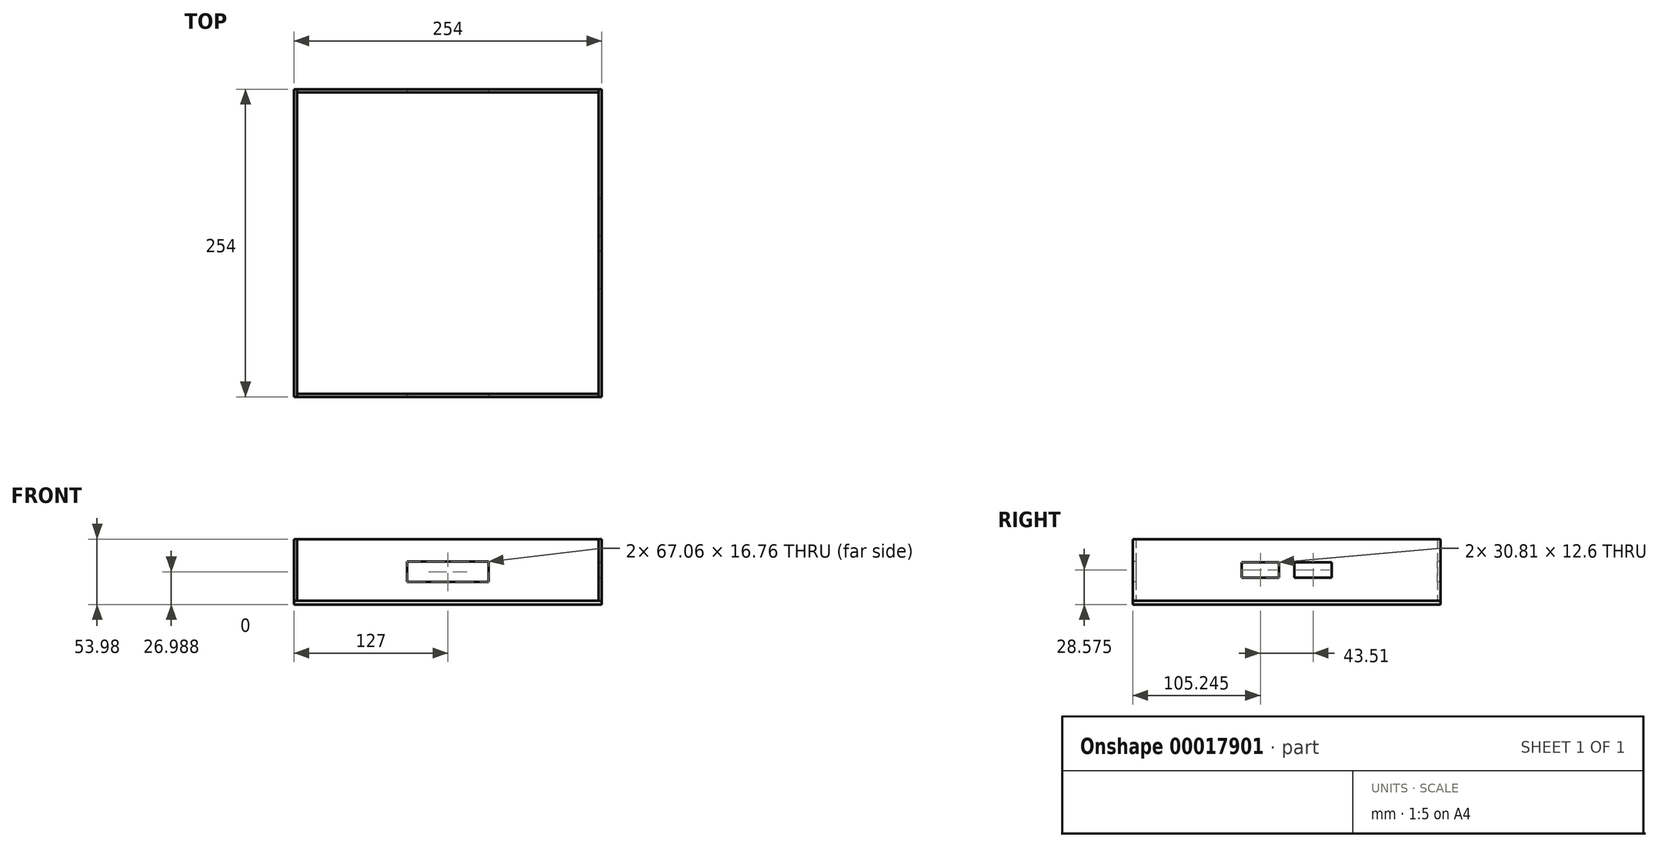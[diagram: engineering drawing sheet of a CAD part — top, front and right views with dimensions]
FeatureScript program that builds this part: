
annotation { "Feature Type Name" : "Feature", "Feature Type Description" : "" }
export const myFeature = defineFeature(function(context is Context, id is Id, definition is map)
    precondition{}
    {
        {
            var Q0;
            Q0=qCreatedBy(makeId("Top.planeOp"),FACE);
            var sketch = newSketch(context, id + "F0", { "sketchPlane" : qUnion([Q0])});
            skLineSegment(sketch, "E0.rect.bottom", {"start": v(-127, 127) * mm, "end": v(127, 127) * mm});
            skLineSegment(sketch, "E0.rect.top", {"start": v(-127, -127) * mm, "end": v(127, -127) * mm});
            skLineSegment(sketch, "E0.rect.left", {"start": v(-127, 127) * mm, "end": v(-127, -127) * mm});
            skLineSegment(sketch, "E0.rect.right", {"start": v(127, 127) * mm, "end": v(127, -127) * mm});
            skPoint(sketch, "E0.rect.middle", {"position": v(0, 0) * mm});
            skSolve(sketch);
        }
        {
            var Q0;
            Q0 = qSketchRegion(id + "F0", true);
            extrude(context, id + "F1", {"entities" : qUnion([Q0]), "depth" : 3.17 * mm});
        }
        {
            var Q0;
            Q0=makeQuery(id+"F1.opExtrude","CAP_FACE",FACE,{"disambiguationData":[OSD([sQuery(id+"F0.wireOp",EDGE,"E0.rect.bottom"),sQuery(id+"F0.wireOp",EDGE,"E0.rect.top"),sQuery(id+"F0.wireOp",EDGE,"E0.rect.left"),sQuery(id+"F0.wireOp",EDGE,"E0.rect.right")])],"isStart":false});
            var sketch = newSketch(context, id + "F2", { "sketchPlane" : qUnion([Q0])});
            skLineSegment(sketch, "E1.bottom", {"start": v(127, 127) * mm, "end": v(124.46, 127) * mm});
            skLineSegment(sketch, "E1.top", {"start": v(127, -127) * mm, "end": v(124.46, -127) * mm});
            skLineSegment(sketch, "E1.left", {"start": v(127, 127) * mm, "end": v(127, -127) * mm});
            skLineSegment(sketch, "E1.right", {"start": v(124.46, 127) * mm, "end": v(124.46, -127) * mm});
            skLineSegment(sketch, "E2.bottom", {"start": v(124.46, -127) * mm, "end": v(-124.46, -127) * mm});
            skLineSegment(sketch, "E2.top", {"start": v(124.46, -124.46) * mm, "end": v(-124.46, -124.46) * mm});
            skLineSegment(sketch, "E2.left", {"start": v(124.46, -127) * mm, "end": v(124.46, -124.46) * mm});
            skLineSegment(sketch, "E2.right", {"start": v(-124.46, -127) * mm, "end": v(-124.46, -124.46) * mm});
            skLineSegment(sketch, "E3.bottom", {"start": v(-127, -127) * mm, "end": v(-124.46, -127) * mm});
            skLineSegment(sketch, "E3.top", {"start": v(-127, 127) * mm, "end": v(-124.46, 127) * mm});
            skLineSegment(sketch, "E3.left", {"start": v(-127, -127) * mm, "end": v(-127, 127) * mm});
            skLineSegment(sketch, "E3.right", {"start": v(-124.46, -127) * mm, "end": v(-124.46, 127) * mm});
            skLineSegment(sketch, "E4.bottom", {"start": v(-124.46, 127) * mm, "end": v(124.46, 127) * mm});
            skLineSegment(sketch, "E4.top", {"start": v(-124.46, 124.46) * mm, "end": v(124.46, 124.46) * mm});
            skLineSegment(sketch, "E4.left", {"start": v(-124.46, 127) * mm, "end": v(-124.46, 124.46) * mm});
            skLineSegment(sketch, "E4.right", {"start": v(124.46, 127) * mm, "end": v(124.46, 124.46) * mm});
            skSolve(sketch);
        }
        {
            var Q0;
            {var subQ2=sQuery(id+"F2.wireOp",EDGE,"E2.bottom");Q0=makeQuery(id+"F2.imprint","IMPRINT",FACE,{"disambiguationData":[TD([[makeQuery(id+"F2.imprint","IMPRINT",EDGE,{"derivedFrom":subQ2}),1.0]])]});}
            extrude(context, id + "F3", {"entities" : qUnion([Q0]), "depth" : 50.8 * mm});
        }
        {
            var Q0;
            {var subQ3=sQuery(id+"F2.wireOp",EDGE,"E3.bottom");Q0=makeQuery(id+"F2.imprint","IMPRINT",FACE,{"disambiguationData":[TD([[makeQuery(id+"F2.imprint","IMPRINT",EDGE,{"derivedFrom":subQ3}),1.0]])]});}
            extrude(context, id + "F4", {"entities" : qUnion([Q0]), "depth" : 50.8 * mm});
        }
        {
            var Q0;
            Q0=makeQuery(id+"F2.imprint","IMPRINT",FACE,{"disambiguationData":[TD([[makeQuery(id+"F2.imprint","IMPRINT",EDGE,{"derivedFrom":sQuery(id+"F2.wireOp",EDGE,"E1.bottom")}),-1.0]])]});
            extrude(context, id + "F5", {"entities" : qUnion([Q0]), "depth" : 50.8 * mm});
        }
        {
            var Q0;
            Q0=makeQuery(id+"F2.imprint","IMPRINT",FACE,{"disambiguationData":[TD([[makeQuery(id+"F2.imprint","IMPRINT",EDGE,{"derivedFrom":sQuery(id+"F2.wireOp",EDGE,"E4.bottom")}),-1.0]])]});
            extrude(context, id + "F6", {"entities" : qUnion([Q0]), "depth" : 50.8 * mm});
        }
        {
            var Q0;
            Q0=qCreatedBy(makeId("Front.planeOp"),FACE);
            var sketch = newSketch(context, id + "F7", { "sketchPlane" : qUnion([Q0])});
            skLineSegment(sketch, "E5.bottom", {"start": v(-33.53, 35.37) * mm, "end": v(33.53, 35.37) * mm});
            skLineSegment(sketch, "E5.top", {"start": v(-33.53, 18.6) * mm, "end": v(33.53, 18.6) * mm});
            skLineSegment(sketch, "E5.left", {"start": v(-33.53, 35.37) * mm, "end": v(-33.53, 18.6) * mm});
            skLineSegment(sketch, "E5.right", {"start": v(33.53, 35.37) * mm, "end": v(33.53, 18.6) * mm});
            skLineSegment(sketch, "E6", {"start": v(0, 35.37) * mm, "end": v(0, 18.6) * mm, "construction": true});
            skLineSegment(sketch, "E7", {"start": v(-33.53, 26.99) * mm, "end": v(33.53, 26.99) * mm, "construction": true});
            skLineSegment(sketch, "E8", {"start": v(0, 0) * mm, "end": v(0, 53.98) * mm, "construction": true});
            skPoint(sketch, "E9", {"position": v(0, 26.99) * mm});
            skSolve(sketch);
        }
        {
            var Q0;
            Q0=makeQuery(id+"F7.imprint","IMPRINT",FACE,{"disambiguationData":[TD([[makeQuery(id+"F7.imprint","IMPRINT",EDGE,{"derivedFrom":sQuery(id+"F7.wireOp",EDGE,"E5.bottom")}),-1.0]])]});
            var Q1;
            Q1=makeQuery(id+"F6.opExtrude","SWEPT_FACE",FACE,{"disambiguationData":[OSD([sQuery(id+"F2.wireOp",EDGE,"E4.bottom")])]});
            extrude(context, id + "F8", {"entities" : qUnion([Q0]), "operationType" : NewBodyOperationType.REMOVE, "endBound" : BoundingType.THROUGH_ALL, "oppositeDirection" : true, "endBoundEntityFace" : qUnion([Q1]), "depth" : 25.4 * mm, "hasSecondDirection" : true, "secondDirectionBound" : SecondDirectionBoundingType.THROUGH_ALL, "secondDirectionOppositeDirection" : false, "secondDirectionDepth" : 25.4 * mm});
        }
        {
            var Q0;
            Q0=makeQuery(id+"F5.opExtrude","SWEPT_FACE",FACE,{"disambiguationData":[OSD([sQuery(id+"F2.wireOp",EDGE,"E1.left")])]});
            var sketch = newSketch(context, id + "F9", { "sketchPlane" : qUnion([Q0])});
            skLineSegment(sketch, "E10.rect.bottom", {"start": v(-6.35, 22.28) * mm, "end": v(-37.16, 22.28) * mm});
            skLineSegment(sketch, "E10.rect.top", {"start": v(-6.35, 34.87) * mm, "end": v(-37.16, 34.87) * mm});
            skLineSegment(sketch, "E10.rect.left", {"start": v(-6.35, 22.28) * mm, "end": v(-6.35, 34.87) * mm});
            skLineSegment(sketch, "E10.rect.right", {"start": v(-37.16, 22.28) * mm, "end": v(-37.16, 34.87) * mm});
            skPoint(sketch, "E10.rect.middle", {"position": v(-21.76, 28.57) * mm});
            skLineSegment(sketch, "E11", {"start": v(-127, 28.58) * mm, "end": v(127, 28.58) * mm, "construction": true});
            skLineSegment(sketch, "E12", {"start": v(0, 53.98) * mm, "end": v(0, 3.18) * mm, "construction": true});
            skLineSegment(sketch, "E13.MirrorCS", {"start": v(6.35, 22.28) * mm, "end": v(37.16, 22.28) * mm});
            skLineSegment(sketch, "E14.MirrorCS", {"start": v(6.35, 22.28) * mm, "end": v(6.35, 34.87) * mm});
            skLineSegment(sketch, "E15.MirrorCS", {"start": v(6.35, 34.87) * mm, "end": v(37.16, 34.87) * mm});
            skLineSegment(sketch, "E16.MirrorCS", {"start": v(37.16, 22.28) * mm, "end": v(37.16, 34.87) * mm});
            skSolve(sketch);
        }
        {
            var Q0;
            Q0 = qSketchRegion(id + "F9", true);
            extrude(context, id + "F10", {"entities" : qUnion([Q0]), "operationType" : NewBodyOperationType.REMOVE, "endBound" : BoundingType.UP_TO_NEXT, "oppositeDirection" : true, "depth" : 25.4 * mm});
        }
    });
